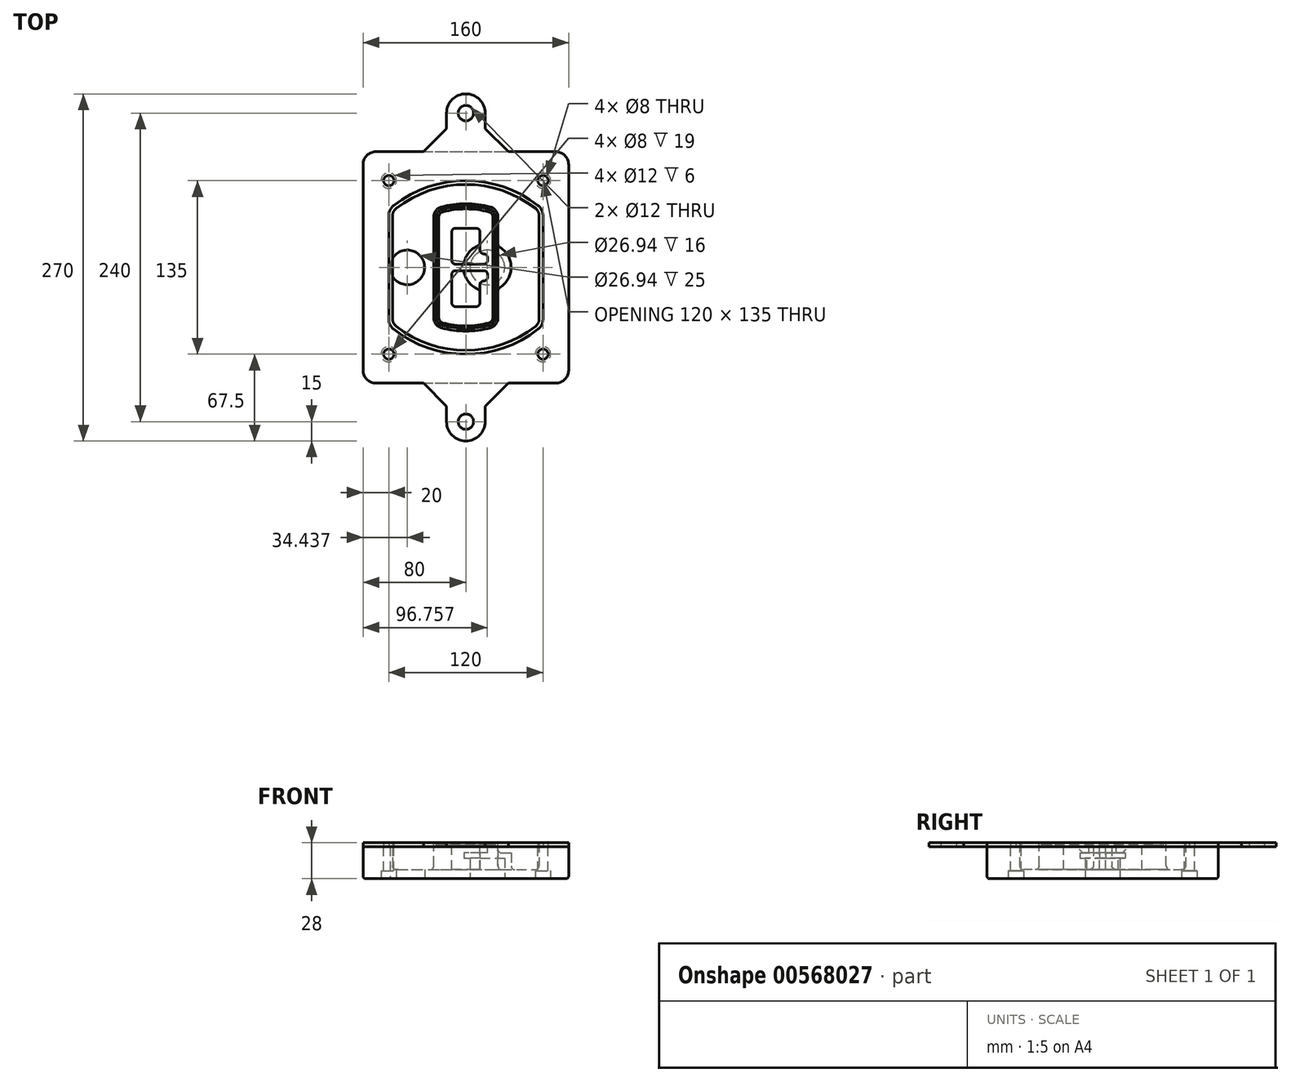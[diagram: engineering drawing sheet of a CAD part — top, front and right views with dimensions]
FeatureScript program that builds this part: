
annotation { "Feature Type Name" : "Feature", "Feature Type Description" : "" }
export const myFeature = defineFeature(function(context is Context, id is Id, definition is map)
    precondition{}
    {
        {
            var Q0;
            Q0=qCreatedBy(makeId("Top.planeOp"),FACE);
            var sketch = newSketch(context, id + "F0", { "sketchPlane" : qUnion([Q0])});
            skPoint(sketch, "E0.rect.middle", {"position": v(0, 0) * mm});
            skLineSegment(sketch, "E1.bottom", {"start": v(-70, -90) * mm, "end": v(70, -90) * mm});
            skLineSegment(sketch, "E1.top", {"start": v(-70, 90) * mm, "end": v(70, 90) * mm});
            skLineSegment(sketch, "E1.left", {"start": v(-80, -80) * mm, "end": v(-80, 80) * mm});
            skLineSegment(sketch, "E1.right", {"start": v(80, -80) * mm, "end": v(80, 80) * mm});
            skLineSegment(sketch, "E2", {"start": v(-80, 90) * mm, "end": v(80, -90) * mm, "construction": true});
            skLineSegment(sketch, "E3", {"start": v(80, 90) * mm, "end": v(-80, -90) * mm, "construction": true});
            skCircle(sketch, "E4", {"center": v(-60, 67.5) * mm, "radius": 4 * mm});
            skCircle(sketch, "E5", {"center": v(60, 67.5) * mm, "radius": 4 * mm});
            skCircle(sketch, "E6", {"center": v(60, -67.5) * mm, "radius": 4 * mm});
            skCircle(sketch, "E7", {"center": v(-60, -67.5) * mm, "radius": 4 * mm});
            skLineSegment(sketch, "E8", {"start": v(-60, 67.5) * mm, "end": v(60, 67.5) * mm, "construction": true});
            skLineSegment(sketch, "E9", {"start": v(60, 67.5) * mm, "end": v(60, -67.5) * mm, "construction": true});
            skLineSegment(sketch, "E10", {"start": v(60, -67.5) * mm, "end": v(-60, -67.5) * mm, "construction": true});
            skLineSegment(sketch, "E11", {"start": v(-60, -67.5) * mm, "end": v(-60, 67.5) * mm, "construction": true});
            skLineSegment(sketch, "E12", {"start": v(-60, 40.3) * mm, "end": v(-60, -40.3) * mm});
            skLineSegment(sketch, "E13", {"start": v(60, 40.3) * mm, "end": v(60, -40.3) * mm});
            skArc(sketch, "E14", {"start": v(56.15, 48.18) * mm, "mid": v(0, 67.5) * mm, "end": v(-56.15, 48.18) * mm});
            skArc(sketch, "E15", {"start": v(-56.15, -48.18) * mm, "mid": v(0, -67.5) * mm, "end": v(56.15, -48.18) * mm});
            skLineSegment(sketch, "E16", {"start": v(-60, 0) * mm, "end": v(60, 0) * mm, "construction": true});
            skPoint(sketch, "E17.visualSharp", {"position": v(-60, -45) * mm});
            skArc(sketch, "E17.filletArc", {"start": v(-60, -40.3) * mm, "mid": v(-58.99, -44.68) * mm, "end": v(-56.15, -48.18) * mm});
            skPoint(sketch, "E18.visualSharp", {"position": v(-60, 45) * mm});
            skArc(sketch, "E18.filletArc", {"start": v(-56.15, 48.18) * mm, "mid": v(-58.99, 44.68) * mm, "end": v(-60, 40.3) * mm});
            skPoint(sketch, "E19.visualSharp", {"position": v(60, 45) * mm});
            skArc(sketch, "E19.filletArc", {"start": v(60, 40.3) * mm, "mid": v(58.99, 44.68) * mm, "end": v(56.15, 48.18) * mm});
            skPoint(sketch, "E20.visualSharp", {"position": v(60, -45) * mm});
            skArc(sketch, "E20.filletArc", {"start": v(56.15, -48.18) * mm, "mid": v(58.99, -44.68) * mm, "end": v(60, -40.3) * mm});
            skPoint(sketch, "E21.visualSharp", {"position": v(-80, 90) * mm});
            skArc(sketch, "E21.filletArc", {"start": v(-70, 90) * mm, "mid": v(-77.07, 87.07) * mm, "end": v(-80, 80) * mm});
            skPoint(sketch, "E22.visualSharp", {"position": v(80, 90) * mm});
            skArc(sketch, "E22.filletArc", {"start": v(80, 80) * mm, "mid": v(77.07, 87.07) * mm, "end": v(70, 90) * mm});
            skPoint(sketch, "E23.visualSharp", {"position": v(80, -90) * mm});
            skArc(sketch, "E23.filletArc", {"start": v(70, -90) * mm, "mid": v(77.07, -87.07) * mm, "end": v(80, -80) * mm});
            skPoint(sketch, "E24.visualSharp", {"position": v(-80, -90) * mm});
            skArc(sketch, "E24.filletArc", {"start": v(-80, -80) * mm, "mid": v(-77.07, -87.07) * mm, "end": v(-70, -90) * mm});
            skArc(sketch, "E25.0", {"start": v(57, 40.3) * mm, "mid": v(56.3, 43.36) * mm, "end": v(54.3, 45.81) * mm});
            skLineSegment(sketch, "E25.1", {"start": v(57, 40.3) * mm, "end": v(57, -40.3) * mm});
            skArc(sketch, "E25.2", {"start": v(54.3, -45.81) * mm, "mid": v(56.3, -43.36) * mm, "end": v(57, -40.3) * mm});
            skArc(sketch, "E25.3", {"start": v(-54.3, -45.81) * mm, "mid": v(0, -64.5) * mm, "end": v(54.3, -45.81) * mm});
            skArc(sketch, "E25.4", {"start": v(-57, -40.3) * mm, "mid": v(-56.3, -43.36) * mm, "end": v(-54.3, -45.81) * mm});
            skArc(sketch, "E25.5", {"start": v(54.3, 45.81) * mm, "mid": v(0, 64.5) * mm, "end": v(-54.3, 45.81) * mm});
            skLineSegment(sketch, "E25.6", {"start": v(-57, 40.3) * mm, "end": v(-57, -40.3) * mm});
            skArc(sketch, "E25.7", {"start": v(-54.3, 45.81) * mm, "mid": v(-56.3, 43.36) * mm, "end": v(-57, 40.3) * mm});
            skArc(sketch, "E26.0", {"start": v(-58.62, 51.33) * mm, "mid": v(-62.58, 46.43) * mm, "end": v(-64, 40.3) * mm});
            skArc(sketch, "E26.1", {"start": v(58.62, 51.33) * mm, "mid": v(0, 71.5) * mm, "end": v(-58.62, 51.33) * mm});
            skArc(sketch, "E26.2", {"start": v(64, 40.3) * mm, "mid": v(62.58, 46.43) * mm, "end": v(58.62, 51.33) * mm});
            skLineSegment(sketch, "E26.3", {"start": v(64, 40.3) * mm, "end": v(64, -40.3) * mm});
            skArc(sketch, "E26.4", {"start": v(58.62, -51.33) * mm, "mid": v(62.58, -46.43) * mm, "end": v(64, -40.3) * mm});
            skLineSegment(sketch, "E26.5", {"start": v(-64, 40.3) * mm, "end": v(-64, -40.3) * mm});
            skArc(sketch, "E26.6", {"start": v(-58.62, -51.33) * mm, "mid": v(0, -71.5) * mm, "end": v(58.62, -51.33) * mm});
            skArc(sketch, "E26.7", {"start": v(-64, -40.3) * mm, "mid": v(-62.58, -46.43) * mm, "end": v(-58.62, -51.33) * mm});
            skSolve(sketch);
        }
        {
            var Q0;
            Q0=makeQuery(id+"F0.imprint","IMPRINT",FACE,{"disambiguationData":[TD([[makeQuery(id+"F0.imprint","IMPRINT",EDGE,{"derivedFrom":sQuery(id+"F0.wireOp",EDGE,"E1.bottom")}),1.0]])]});
            var Q1;
            Q1=makeQuery(id+"F0.imprint","IMPRINT",FACE,{"disambiguationData":[TD([[makeQuery(id+"F0.imprint","IMPRINT",EDGE,{"derivedFrom":sQuery(id+"F0.wireOp",EDGE,"E12")}),1.0]])]});
            var Q2;
            Q2=makeQuery(id+"F0.imprint","IMPRINT",FACE,{"disambiguationData":[TD([[makeQuery(id+"F0.imprint","IMPRINT",EDGE,{"derivedFrom":sQuery(id+"F0.wireOp",EDGE,"E25.0")}),1.0]])]});
            var Q3;
            Q3=makeQuery(id+"F0.imprint","IMPRINT",FACE,{"disambiguationData":[TD([[makeQuery(id+"F0.imprint","IMPRINT",EDGE,{"derivedFrom":sQuery(id+"F0.wireOp",EDGE,"E12")}),-1.0]])]});
            extrude(context, id + "F1", {"entities" : qUnion([Q0, Q1, Q2, Q3]), "oppositeDirection" : true, "depth" : 25 * mm});
        }
        {
            var Q0;
            Q0=makeQuery(id+"F0.imprint","IMPRINT",FACE,{"disambiguationData":[TD([[makeQuery(id+"F0.imprint","IMPRINT",EDGE,{"derivedFrom":sQuery(id+"F0.wireOp",EDGE,"E12")}),1.0]])]});
            extrude(context, id + "F2", {"entities" : qUnion([Q0]), "operationType" : NewBodyOperationType.ADD, "depth" : 3 * mm});
        }
        {
            var Q0;
            Q0=makeQuery(id+"F0.imprint","IMPRINT",FACE,{"disambiguationData":[TD([[makeQuery(id+"F0.imprint","IMPRINT",EDGE,{"derivedFrom":sQuery(id+"F0.wireOp",EDGE,"E25.0")}),1.0]])]});
            extrude(context, id + "F3", {"entities" : qUnion([Q0]), "operationType" : NewBodyOperationType.REMOVE, "oppositeDirection" : true, "depth" : 18 * mm});
        }
        {
            var Q0;
            Q0=makeQuery(id+"F2.opExtrude","CAP_FACE",FACE,{"disambiguationData":[OSD([sQuery(id+"F0.wireOp",EDGE,"E12"),sQuery(id+"F0.wireOp",EDGE,"E13"),sQuery(id+"F0.wireOp",EDGE,"E14"),sQuery(id+"F0.wireOp",EDGE,"E15"),sQuery(id+"F0.wireOp",EDGE,"E17.filletArc"),sQuery(id+"F0.wireOp",EDGE,"E18.filletArc"),sQuery(id+"F0.wireOp",EDGE,"E19.filletArc"),sQuery(id+"F0.wireOp",EDGE,"E20.filletArc"),sQuery(id+"F0.wireOp",EDGE,"E25.0"),sQuery(id+"F0.wireOp",EDGE,"E25.1"),sQuery(id+"F0.wireOp",EDGE,"E25.2"),sQuery(id+"F0.wireOp",EDGE,"E25.3"),sQuery(id+"F0.wireOp",EDGE,"E25.4"),sQuery(id+"F0.wireOp",EDGE,"E25.5"),sQuery(id+"F0.wireOp",EDGE,"E25.6"),sQuery(id+"F0.wireOp",EDGE,"E25.7")])],"isStart":false});
            var sketch = newSketch(context, id + "F4", { "sketchPlane" : qUnion([Q0])});
            skArc(sketch, "E27.0", {"start": v(-19.08, -46.97) * mm, "mid": v(0, -49.5) * mm, "end": v(19.08, -46.97) * mm});
            skArc(sketch, "E28.0", {"start": v(19.08, 46.97) * mm, "mid": v(0, 49.5) * mm, "end": v(-19.08, 46.97) * mm});
            skLineSegment(sketch, "E29", {"start": v(-25, 39.25) * mm, "end": v(-25, -39.25) * mm});
            skLineSegment(sketch, "E30", {"start": v(25, 39.25) * mm, "end": v(25, -39.25) * mm});
            skLineSegment(sketch, "E31", {"start": v(-25, 45.1) * mm, "end": v(25, 45.1) * mm, "construction": true});
            skLineSegment(sketch, "E32", {"start": v(-25, -45.1) * mm, "end": v(25, -45.1) * mm, "construction": true});
            skPoint(sketch, "E33.visualSharp", {"position": v(-25, 45.1) * mm});
            skArc(sketch, "E33.filletArc", {"start": v(-19.08, 46.97) * mm, "mid": v(-23.35, 44.11) * mm, "end": v(-25, 39.25) * mm});
            skPoint(sketch, "E34.visualSharp", {"position": v(25, 45.1) * mm});
            skArc(sketch, "E34.filletArc", {"start": v(25, 39.25) * mm, "mid": v(23.35, 44.11) * mm, "end": v(19.08, 46.97) * mm});
            skPoint(sketch, "E35.visualSharp", {"position": v(25, -45.1) * mm});
            skArc(sketch, "E35.filletArc", {"start": v(19.08, -46.97) * mm, "mid": v(23.35, -44.11) * mm, "end": v(25, -39.25) * mm});
            skPoint(sketch, "E36.visualSharp", {"position": v(-25, -45.1) * mm});
            skArc(sketch, "E36.filletArc", {"start": v(-25, -39.25) * mm, "mid": v(-23.35, -44.11) * mm, "end": v(-19.08, -46.97) * mm});
            skArc(sketch, "E37.0", {"start": v(54.3, 45.81) * mm, "mid": v(0, 64.5) * mm, "end": v(-54.3, 45.81) * mm});
            skArc(sketch, "E37.1", {"start": v(-54.3, 45.81) * mm, "mid": v(-56.3, 43.36) * mm, "end": v(-57, 40.3) * mm});
            skLineSegment(sketch, "E37.2", {"start": v(-57, 40.3) * mm, "end": v(-57, -40.3) * mm});
            skArc(sketch, "E37.3", {"start": v(-57, -40.3) * mm, "mid": v(-56.3, -43.36) * mm, "end": v(-54.3, -45.81) * mm});
            skArc(sketch, "E37.4", {"start": v(-54.3, -45.81) * mm, "mid": v(0, -64.5) * mm, "end": v(54.3, -45.81) * mm});
            skArc(sketch, "E37.5", {"start": v(54.3, -45.81) * mm, "mid": v(56.3, -43.36) * mm, "end": v(57, -40.3) * mm});
            skLineSegment(sketch, "E37.6", {"start": v(57, 40.3) * mm, "end": v(57, -40.3) * mm});
            skArc(sketch, "E37.7", {"start": v(57, 40.3) * mm, "mid": v(56.3, 43.36) * mm, "end": v(54.3, 45.81) * mm});
            skLineSegment(sketch, "E38.0", {"start": v(23, 39.25) * mm, "end": v(23, -39.25) * mm});
            skArc(sketch, "E38.1", {"start": v(18.56, -45.04) * mm, "mid": v(21.76, -42.9) * mm, "end": v(23, -39.25) * mm});
            skArc(sketch, "E38.2", {"start": v(-18.56, -45.04) * mm, "mid": v(0, -47.5) * mm, "end": v(18.56, -45.04) * mm});
            skArc(sketch, "E38.3", {"start": v(-23, -39.25) * mm, "mid": v(-21.76, -42.9) * mm, "end": v(-18.56, -45.04) * mm});
            skLineSegment(sketch, "E38.4", {"start": v(-23, 39.25) * mm, "end": v(-23, -39.25) * mm});
            skArc(sketch, "E38.5", {"start": v(23, 39.25) * mm, "mid": v(21.76, 42.9) * mm, "end": v(18.56, 45.04) * mm});
            skArc(sketch, "E38.6", {"start": v(-18.56, 45.04) * mm, "mid": v(-21.76, 42.9) * mm, "end": v(-23, 39.25) * mm});
            skArc(sketch, "E38.7", {"start": v(18.56, 45.04) * mm, "mid": v(0, 47.5) * mm, "end": v(-18.56, 45.04) * mm});
            skArc(sketch, "E39.0", {"start": v(21, 39.25) * mm, "mid": v(20.18, 41.68) * mm, "end": v(18.04, 43.1) * mm});
            skLineSegment(sketch, "E39.1", {"start": v(21, 39.25) * mm, "end": v(21, -39.25) * mm});
            skArc(sketch, "E39.2", {"start": v(18.04, -43.1) * mm, "mid": v(20.18, -41.68) * mm, "end": v(21, -39.25) * mm});
            skArc(sketch, "E39.3", {"start": v(-18.04, -43.1) * mm, "mid": v(0, -45.5) * mm, "end": v(18.04, -43.1) * mm});
            skArc(sketch, "E39.4", {"start": v(-21, -39.25) * mm, "mid": v(-20.18, -41.68) * mm, "end": v(-18.04, -43.1) * mm});
            skArc(sketch, "E39.5", {"start": v(18.04, 43.1) * mm, "mid": v(0, 45.5) * mm, "end": v(-18.04, 43.1) * mm});
            skLineSegment(sketch, "E39.6", {"start": v(-21, 39.25) * mm, "end": v(-21, -39.25) * mm});
            skArc(sketch, "E39.7", {"start": v(-18.04, 43.1) * mm, "mid": v(-20.18, 41.68) * mm, "end": v(-21, 39.25) * mm});
            skLineSegment(sketch, "E40", {"start": v(-25, 0) * mm, "end": v(25, 0) * mm, "construction": true});
            skLineSegment(sketch, "E41", {"start": v(-11, 5.5) * mm, "end": v(-11, 27.5) * mm});
            skLineSegment(sketch, "E42", {"start": v(-8, 30.5) * mm, "end": v(8, 30.5) * mm});
            skLineSegment(sketch, "E43", {"start": v(11, 27.5) * mm, "end": v(11, 13.5) * mm});
            skLineSegment(sketch, "E44", {"start": v(14, 10.5) * mm, "end": v(14, 10.5) * mm});
            skLineSegment(sketch, "E45", {"start": v(17, 7.5) * mm, "end": v(17, 5.5) * mm});
            skLineSegment(sketch, "E46", {"start": v(14, 2.5) * mm, "end": v(-8, 2.5) * mm});
            skPoint(sketch, "E47.visualSharp", {"position": v(-11, 30.5) * mm});
            skArc(sketch, "E47.filletArc", {"start": v(-8, 30.5) * mm, "mid": v(-10.12, 29.62) * mm, "end": v(-11, 27.5) * mm});
            skPoint(sketch, "E48.visualSharp", {"position": v(11, 30.5) * mm});
            skArc(sketch, "E48.filletArc", {"start": v(11, 27.5) * mm, "mid": v(10.12, 29.62) * mm, "end": v(8, 30.5) * mm});
            skPoint(sketch, "E49.visualSharp", {"position": v(11, 10.5) * mm});
            skArc(sketch, "E49.filletArc", {"start": v(11, 13.5) * mm, "mid": v(11.88, 11.38) * mm, "end": v(14, 10.5) * mm});
            skPoint(sketch, "E50.visualSharp", {"position": v(17, 10.5) * mm});
            skArc(sketch, "E50.filletArc", {"start": v(17, 7.5) * mm, "mid": v(16.12, 9.62) * mm, "end": v(14, 10.5) * mm});
            skPoint(sketch, "E51.visualSharp", {"position": v(17, 2.5) * mm});
            skArc(sketch, "E51.filletArc", {"start": v(14, 2.5) * mm, "mid": v(16.12, 3.38) * mm, "end": v(17, 5.5) * mm});
            skPoint(sketch, "E52.visualSharp", {"position": v(-11, 2.5) * mm});
            skArc(sketch, "E52.filletArc", {"start": v(-11, 5.5) * mm, "mid": v(-10.12, 3.38) * mm, "end": v(-8, 2.5) * mm});
            skLineSegment(sketch, "E53.0.MirrorCS", {"start": v(14, -2.5) * mm, "end": v(-8, -2.5) * mm});
            skArc(sketch, "E54.0.MirrorCS", {"start": v(-11, -5.5) * mm, "mid": v(-10.12, -3.38) * mm, "end": v(-8, -2.5) * mm});
            skLineSegment(sketch, "E55.0.MirrorCS", {"start": v(-11, -5.5) * mm, "end": v(-11, -27.5) * mm});
            skArc(sketch, "E56.0.MirrorCS", {"start": v(-8, -30.5) * mm, "mid": v(-10.12, -29.62) * mm, "end": v(-11, -27.5) * mm});
            skLineSegment(sketch, "E57.0.MirrorCS", {"start": v(-8, -30.5) * mm, "end": v(8, -30.5) * mm});
            skArc(sketch, "E58.0.MirrorCS", {"start": v(11, -27.5) * mm, "mid": v(10.12, -29.62) * mm, "end": v(8, -30.5) * mm});
            skLineSegment(sketch, "E59.0.MirrorCS", {"start": v(11, -27.5) * mm, "end": v(11, -13.5) * mm});
            skArc(sketch, "E60.0.MirrorCS", {"start": v(11, -13.5) * mm, "mid": v(11.88, -11.38) * mm, "end": v(14, -10.5) * mm});
            skArc(sketch, "E61.0.MirrorCS", {"start": v(17, -7.5) * mm, "mid": v(16.12, -9.62) * mm, "end": v(14, -10.5) * mm});
            skLineSegment(sketch, "E62.0.MirrorCS", {"start": v(17, -7.5) * mm, "end": v(17, -5.5) * mm});
            skArc(sketch, "E63.0.MirrorCS", {"start": v(14, -2.5) * mm, "mid": v(16.12, -3.38) * mm, "end": v(17, -5.5) * mm});
            skSolve(sketch);
        }
        {
            var Q0;
            Q0=makeQuery(id+"F4.imprint","IMPRINT",FACE,{"disambiguationData":[TD([[makeQuery(id+"F4.imprint","IMPRINT",EDGE,{"derivedFrom":sQuery(id+"F4.wireOp",EDGE,"E27.0")}),1.0]])]});
            var Q1;
            Q1=makeQuery(id+"F4.imprint","IMPRINT",FACE,{"disambiguationData":[TD([[makeQuery(id+"F4.imprint","IMPRINT",EDGE,{"derivedFrom":sQuery(id+"F4.wireOp",EDGE,"E38.0")}),-1.0]])]});
            var Q2;
            Q2=makeQuery(id+"F4.imprint","IMPRINT",FACE,{"disambiguationData":[TD([[makeQuery(id+"F4.imprint","IMPRINT",EDGE,{"derivedFrom":sQuery(id+"F4.wireOp",EDGE,"E39.0")}),1.0]])]});
            extrude(context, id + "F5", {"entities" : qUnion([Q0, Q1, Q2]), "operationType" : NewBodyOperationType.ADD, "endBound" : BoundingType.UP_TO_NEXT, "oppositeDirection" : true, "depth" : 25 * mm});
        }
        {
            var Q0;
            Q0=makeQuery(id+"F4.imprint","IMPRINT",FACE,{"disambiguationData":[TD([[makeQuery(id+"F4.imprint","IMPRINT",EDGE,{"derivedFrom":sQuery(id+"F4.wireOp",EDGE,"E38.0")}),-1.0]])]});
            extrude(context, id + "F6", {"entities" : qUnion([Q0]), "operationType" : NewBodyOperationType.REMOVE, "oppositeDirection" : true, "depth" : 2 * mm});
        }
        {
            var Q0;
            Q0=makeQuery(id+"F1.opExtrude","CAP_FACE",FACE,{"disambiguationData":[OSD([sQuery(id+"F0.wireOp",EDGE,"E1.bottom"),sQuery(id+"F0.wireOp",EDGE,"E1.top"),sQuery(id+"F0.wireOp",EDGE,"E1.left"),sQuery(id+"F0.wireOp",EDGE,"E1.right"),sQuery(id+"F0.wireOp",EDGE,"E4"),sQuery(id+"F0.wireOp",EDGE,"E5"),sQuery(id+"F0.wireOp",EDGE,"E6"),sQuery(id+"F0.wireOp",EDGE,"E7"),sQuery(id+"F0.wireOp",EDGE,"E21.filletArc"),sQuery(id+"F0.wireOp",EDGE,"E22.filletArc"),sQuery(id+"F0.wireOp",EDGE,"E23.filletArc"),sQuery(id+"F0.wireOp",EDGE,"E24.filletArc")])],"isStart":false});
            var sketch = newSketch(context, id + "F7", { "sketchPlane" : qUnion([Q0])});
            skCircle(sketch, "E64", {"center": v(16.76, 0) * mm, "radius": 13.47 * mm});
            skCircle(sketch, "E65", {"center": v(-45.56, 0) * mm, "radius": 13.47 * mm});
            skLineSegment(sketch, "E66", {"start": v(80, 0) * mm, "end": v(-80, 0) * mm});
            skCircle(sketch, "E67", {"center": v(16.76, 0) * mm, "radius": 18.47 * mm});
            skCircle(sketch, "E68", {"center": v(60, -67.5) * mm, "radius": 6 * mm});
            skCircle(sketch, "E69", {"center": v(-60, -67.5) * mm, "radius": 6 * mm});
            skCircle(sketch, "E70", {"center": v(-60, 67.5) * mm, "radius": 6 * mm});
            skCircle(sketch, "E71", {"center": v(60, 67.5) * mm, "radius": 6 * mm});
            skSolve(sketch);
        }
        {
            var Q0;
            {var subQ1=sQuery(id+"F7.wireOp",EDGE,"E66");var subQ4=sQuery(id+"F7.wireOp",EDGE,"E64");var subQ6=makeQuery(id+"F7.imprint","INTERSECT",VERTEX,{"disambiguationData":[OD(0.0)],"derivedFrom":[subQ4,subQ1]});Q0=makeQuery(id+"F7.imprint","IMPRINT",FACE,{"disambiguationData":[TD([[makeQuery(id+"F7.imprint","IMPRINT",EDGE,{"disambiguationData":[TD([[subQ6,-1.0]])],"derivedFrom":subQ4}),-1.0]])]});}
            var Q1;
            {var subQ0=sQuery(id+"F7.wireOp",EDGE,"E66");var subQ1=sQuery(id+"F7.wireOp",EDGE,"E64");var subQ3=makeQuery(id+"F7.imprint","INTERSECT",VERTEX,{"disambiguationData":[OD(0.0)],"derivedFrom":[subQ1,subQ0]});Q1=makeQuery(id+"F7.imprint","IMPRINT",FACE,{"disambiguationData":[TD([[makeQuery(id+"F7.imprint","IMPRINT",EDGE,{"disambiguationData":[TD([[subQ3,-1.0]])],"derivedFrom":subQ1}),1.0]])]});}
            var Q2;
            {var subQ0=sQuery(id+"F7.wireOp",EDGE,"E66");var subQ1=sQuery(id+"F7.wireOp",EDGE,"E64");var subQ3=makeQuery(id+"F7.imprint","INTERSECT",VERTEX,{"disambiguationData":[OD(0.0)],"derivedFrom":[subQ1,subQ0]});Q2=makeQuery(id+"F7.imprint","IMPRINT",FACE,{"disambiguationData":[TD([[makeQuery(id+"F7.imprint","IMPRINT",EDGE,{"disambiguationData":[TD([[subQ3,1.0]])],"derivedFrom":subQ1}),1.0]])]});}
            var Q3;
            {var subQ1=sQuery(id+"F7.wireOp",EDGE,"E66");var subQ4=sQuery(id+"F7.wireOp",EDGE,"E64");var subQ6=makeQuery(id+"F7.imprint","INTERSECT",VERTEX,{"disambiguationData":[OD(0.0)],"derivedFrom":[subQ4,subQ1]});Q3=makeQuery(id+"F7.imprint","IMPRINT",FACE,{"disambiguationData":[TD([[makeQuery(id+"F7.imprint","IMPRINT",EDGE,{"disambiguationData":[TD([[subQ6,1.0]])],"derivedFrom":subQ4}),-1.0]])]});}
            extrude(context, id + "F8", {"entities" : qUnion([Q0, Q1, Q2, Q3]), "operationType" : NewBodyOperationType.ADD, "oppositeDirection" : true, "depth" : 20 * mm});
        }
        {
            var Q0;
            {var subQ0=sQuery(id+"F7.wireOp",EDGE,"E66");var subQ1=sQuery(id+"F7.wireOp",EDGE,"E64");var subQ3=makeQuery(id+"F7.imprint","INTERSECT",VERTEX,{"disambiguationData":[OD(0.0)],"derivedFrom":[subQ1,subQ0]});Q0=makeQuery(id+"F7.imprint","IMPRINT",FACE,{"disambiguationData":[TD([[makeQuery(id+"F7.imprint","IMPRINT",EDGE,{"disambiguationData":[TD([[subQ3,-1.0]])],"derivedFrom":subQ1}),1.0]])]});}
            var Q1;
            {var subQ0=sQuery(id+"F7.wireOp",EDGE,"E66");var subQ1=sQuery(id+"F7.wireOp",EDGE,"E64");var subQ3=makeQuery(id+"F7.imprint","INTERSECT",VERTEX,{"disambiguationData":[OD(0.0)],"derivedFrom":[subQ1,subQ0]});Q1=makeQuery(id+"F7.imprint","IMPRINT",FACE,{"disambiguationData":[TD([[makeQuery(id+"F7.imprint","IMPRINT",EDGE,{"disambiguationData":[TD([[subQ3,1.0]])],"derivedFrom":subQ1}),1.0]])]});}
            extrude(context, id + "F9", {"entities" : qUnion([Q0, Q1]), "operationType" : NewBodyOperationType.REMOVE, "oppositeDirection" : true, "depth" : 16 * mm});
        }
        {
            var Q0;
            {var subQ0=sQuery(id+"F7.wireOp",EDGE,"E66");var subQ1=sQuery(id+"F7.wireOp",EDGE,"E65");var subQ3=makeQuery(id+"F7.imprint","INTERSECT",VERTEX,{"disambiguationData":[OD(0.0)],"derivedFrom":[subQ1,subQ0]});Q0=makeQuery(id+"F7.imprint","IMPRINT",FACE,{"disambiguationData":[TD([[makeQuery(id+"F7.imprint","IMPRINT",EDGE,{"disambiguationData":[TD([[subQ3,-1.0]])],"derivedFrom":subQ1}),1.0]])]});}
            var Q1;
            {var subQ0=sQuery(id+"F7.wireOp",EDGE,"E66");var subQ1=sQuery(id+"F7.wireOp",EDGE,"E65");var subQ3=makeQuery(id+"F7.imprint","INTERSECT",VERTEX,{"disambiguationData":[OD(0.0)],"derivedFrom":[subQ1,subQ0]});Q1=makeQuery(id+"F7.imprint","IMPRINT",FACE,{"disambiguationData":[TD([[makeQuery(id+"F7.imprint","IMPRINT",EDGE,{"disambiguationData":[TD([[subQ3,1.0]])],"derivedFrom":subQ1}),1.0]])]});}
            extrude(context, id + "F10", {"entities" : qUnion([Q0, Q1]), "operationType" : NewBodyOperationType.REMOVE, "oppositeDirection" : true, "depth" : 25 * mm});
        }
        {
            var Q0;
            Q0=makeQuery(id+"F7.imprint","IMPRINT",FACE,{"disambiguationData":[TD([[makeQuery(id+"F7.imprint","IMPRINT",EDGE,{"derivedFrom":sQuery(id+"F7.wireOp",EDGE,"E68")}),1.0]])]});
            var Q1;
            Q1=makeQuery(id+"F7.imprint","IMPRINT",FACE,{"disambiguationData":[TD([[makeQuery(id+"F7.imprint","IMPRINT",EDGE,{"derivedFrom":makeQuery(id+"F1.opExtrude","CAP_EDGE",EDGE,{"disambiguationData":[OSD([sQuery(id+"F0.wireOp",EDGE,"E5")])],"isStart":false})}),-1.0]])]});
            var Q2;
            Q2=makeQuery(id+"F7.imprint","IMPRINT",FACE,{"disambiguationData":[TD([[makeQuery(id+"F7.imprint","IMPRINT",EDGE,{"derivedFrom":sQuery(id+"F7.wireOp",EDGE,"E69")}),1.0]])]});
            var Q3;
            Q3=makeQuery(id+"F7.imprint","IMPRINT",FACE,{"disambiguationData":[TD([[makeQuery(id+"F7.imprint","IMPRINT",EDGE,{"derivedFrom":makeQuery(id+"F1.opExtrude","CAP_EDGE",EDGE,{"disambiguationData":[OSD([sQuery(id+"F0.wireOp",EDGE,"E4")])],"isStart":false})}),-1.0]])]});
            var Q4;
            Q4=makeQuery(id+"F7.imprint","IMPRINT",FACE,{"disambiguationData":[TD([[makeQuery(id+"F7.imprint","IMPRINT",EDGE,{"derivedFrom":sQuery(id+"F7.wireOp",EDGE,"E70")}),1.0]])]});
            var Q5;
            Q5=makeQuery(id+"F7.imprint","IMPRINT",FACE,{"disambiguationData":[TD([[makeQuery(id+"F7.imprint","IMPRINT",EDGE,{"derivedFrom":makeQuery(id+"F1.opExtrude","CAP_EDGE",EDGE,{"disambiguationData":[OSD([sQuery(id+"F0.wireOp",EDGE,"E7")])],"isStart":false})}),-1.0]])]});
            var Q6;
            Q6=makeQuery(id+"F7.imprint","IMPRINT",FACE,{"disambiguationData":[TD([[makeQuery(id+"F7.imprint","IMPRINT",EDGE,{"derivedFrom":sQuery(id+"F7.wireOp",EDGE,"E71")}),1.0]])]});
            var Q7;
            Q7=makeQuery(id+"F7.imprint","IMPRINT",FACE,{"disambiguationData":[TD([[makeQuery(id+"F7.imprint","IMPRINT",EDGE,{"derivedFrom":makeQuery(id+"F1.opExtrude","CAP_EDGE",EDGE,{"disambiguationData":[OSD([sQuery(id+"F0.wireOp",EDGE,"E6")])],"isStart":false})}),-1.0]])]});
            extrude(context, id + "F11", {"entities" : qUnion([Q0, Q1, Q2, Q3, Q4, Q5, Q6, Q7]), "operationType" : NewBodyOperationType.REMOVE, "oppositeDirection" : true, "depth" : 6 * mm});
        }
        {
            var Q0;
            Q0=makeQuery(id+"F9.boolean.opBoolean","COPY",FACE,{"derivedFrom":makeQuery(id+"F9.opExtrude","CAP_FACE",FACE,{"disambiguationData":[OSD([sQuery(id+"F7.wireOp",EDGE,"E64")])],"isStart":false})});
            var sketch = newSketch(context, id + "F12", { "sketchPlane" : qUnion([Q0])});
            skArc(sketch, "E72.0", {"start": v(11, 17.55) * mm, "mid": v(2.57, 11.82) * mm, "end": v(-1.54, 2.5) * mm});
            skArc(sketch, "E72.1", {"start": v(-1.54, -2.5) * mm, "mid": v(2.57, -11.82) * mm, "end": v(11, -17.55) * mm});
            skLineSegment(sketch, "E73", {"start": v(-1.54, -2.5) * mm, "end": v(14, -2.5) * mm});
            skLineSegment(sketch, "E74.0", {"start": v(14, 2.5) * mm, "end": v(-1.54, 2.5) * mm});
            skArc(sketch, "E74.1", {"start": v(14, 2.5) * mm, "mid": v(16.12, 3.38) * mm, "end": v(17, 5.5) * mm});
            skLineSegment(sketch, "E74.2", {"start": v(17, 7.5) * mm, "end": v(17, 5.5) * mm});
            skArc(sketch, "E74.3", {"start": v(17, 7.5) * mm, "mid": v(16.12, 9.62) * mm, "end": v(14, 10.5) * mm});
            skArc(sketch, "E74.4", {"start": v(11, 13.5) * mm, "mid": v(11.88, 11.38) * mm, "end": v(14, 10.5) * mm});
            skLineSegment(sketch, "E74.5", {"start": v(11, 17.55) * mm, "end": v(11, 13.5) * mm});
            skLineSegment(sketch, "E74.7", {"start": v(14, -2.5) * mm, "end": v(-1.54, -2.5) * mm});
            skArc(sketch, "E74.8", {"start": v(14, -2.5) * mm, "mid": v(16.12, -3.38) * mm, "end": v(17, -5.5) * mm});
            skLineSegment(sketch, "E74.9", {"start": v(17, -7.5) * mm, "end": v(17, -5.5) * mm});
            skArc(sketch, "E74.10", {"start": v(17, -7.5) * mm, "mid": v(16.12, -9.62) * mm, "end": v(14, -10.5) * mm});
            skArc(sketch, "E74.11", {"start": v(11, -13.5) * mm, "mid": v(11.88, -11.38) * mm, "end": v(14, -10.5) * mm});
            skLineSegment(sketch, "E74.12", {"start": v(11, -17.55) * mm, "end": v(11, -13.5) * mm});
            skPoint(sketch, "E75.orphan", {"position": v(11, -27.5) * mm});
            skPoint(sketch, "E76.orphan", {"position": v(-8, -2.5) * mm});
            skPoint(sketch, "E77.orphan", {"position": v(-8, 2.5) * mm});
            skPoint(sketch, "E78.orphan", {"position": v(11, 27.5) * mm});
            skSolve(sketch);
        }
        {
            var Q0;
            {var subQ7=sQuery(id+"F12.wireOp",EDGE,"E72.0");var subQ14=sQuery(id+"F12.wireOp",EDGE,"E72.1");var subQ16=sQuery(id+"F12.wireOp",EDGE,"E74.1");var subQ18=sQuery(id+"F12.wireOp",EDGE,"E74.8");Q0=qUnion([makeQuery(id+"F12.imprint","IMPRINT",FACE,{"disambiguationData":[TD([[makeQuery(id+"F12.imprint","IMPRINT",EDGE,{"derivedFrom":subQ7}),1.0]])]}),makeQuery(id+"F12.imprint","IMPRINT",FACE,{"disambiguationData":[TD([[makeQuery(id+"F12.imprint","IMPRINT",EDGE,{"derivedFrom":subQ14}),1.0]])]}),makeQuery(id+"F12.imprint","IMPRINT",FACE,{"disambiguationData":[TD([[makeQuery(id+"F12.imprint","IMPRINT",EDGE,{"derivedFrom":subQ16}),1.0]])]}),makeQuery(id+"F12.imprint","IMPRINT",FACE,{"disambiguationData":[TD([[makeQuery(id+"F12.imprint","IMPRINT",EDGE,{"derivedFrom":subQ18}),-1.0]])]})]);}
            var Q1;
            Q1=makeQuery(id+"F5.boolean.opBoolean","SPLIT",FACE,{"disambiguationData":[TD([makeQuery(id+"F5.opExtrude","SWEPT_FACE",FACE,{"disambiguationData":[OSD([sQuery(id+"F4.wireOp",EDGE,"E41")])]})])],"derivedFrom":makeQuery(id+"F3.boolean.opBoolean","COPY",FACE,{"derivedFrom":makeQuery(id+"F3.opExtrude","CAP_FACE",FACE,{"disambiguationData":[OSD([sQuery(id+"F0.wireOp",EDGE,"E25.0"),sQuery(id+"F0.wireOp",EDGE,"E25.1"),sQuery(id+"F0.wireOp",EDGE,"E25.2"),sQuery(id+"F0.wireOp",EDGE,"E25.3"),sQuery(id+"F0.wireOp",EDGE,"E25.4"),sQuery(id+"F0.wireOp",EDGE,"E25.5"),sQuery(id+"F0.wireOp",EDGE,"E25.6"),sQuery(id+"F0.wireOp",EDGE,"E25.7")])],"isStart":false})})});
            extrude(context, id + "F13", {"entities" : qUnion([Q0]), "operationType" : NewBodyOperationType.REMOVE, "endBound" : BoundingType.UP_TO_SURFACE, "endBoundEntityFace" : qUnion([Q1]), "depth" : 25 * mm});
        }
        {
            var Q0;
            Q0=makeQuery(id+"F3.boolean.opBoolean","COPY",EDGE,{"derivedFrom":makeQuery(id+"F3.opExtrude","CAP_EDGE",EDGE,{"disambiguationData":[OSD([sQuery(id+"F0.wireOp",EDGE,"E25.6")])],"isStart":false})});
            var Q1;
            Q1=makeQuery(id+"F8.boolean.opBoolean","INTERSECT",EDGE,{"derivedFrom":[makeQuery(id+"F5.opExtrude","SWEPT_FACE",FACE,{"disambiguationData":[OSD([sQuery(id+"F4.wireOp",EDGE,"E30")])]}),makeQuery(id+"F8.opExtrude","CAP_FACE",FACE,{"disambiguationData":[OSD([sQuery(id+"F7.wireOp",EDGE,"E67")])],"isStart":false})]});
            var Q2;
            Q2=makeQuery(id+"F8.boolean.opBoolean","INTERSECT",EDGE,{"disambiguationData":[OD(1.0)],"derivedFrom":[makeQuery(id+"F5.opExtrude","SWEPT_FACE",FACE,{"disambiguationData":[OSD([sQuery(id+"F4.wireOp",EDGE,"E30")])]}),makeQuery(id+"F8.opExtrude","SWEPT_FACE",FACE,{"disambiguationData":[OSD([sQuery(id+"F7.wireOp",EDGE,"E67")])]})]});
            var Q3;
            {var subQ0=sQuery(id+"F4.wireOp",EDGE,"E30");Q3=makeQuery(id+"F8.boolean.opBoolean","SPLIT",EDGE,{"disambiguationData":[TD([makeQuery(id+"F5.opExtrude","SWEPT_FACE",FACE,{"disambiguationData":[OSD([sQuery(id+"F4.wireOp",EDGE,"E35.filletArc")])]})])],"derivedFrom":makeQuery(id+"F5.opExtrude","CAP_EDGE",EDGE,{"disambiguationData":[OSD([subQ0])],"isStart":false})});}
            var Q4;
            {var subQ0=sQuery(id+"F0.wireOp",EDGE,"E25.7");var subQ1=sQuery(id+"F0.wireOp",EDGE,"E25.1");var subQ2=sQuery(id+"F0.wireOp",EDGE,"E25.6");var subQ3=sQuery(id+"F0.wireOp",EDGE,"E25.5");var subQ4=sQuery(id+"F0.wireOp",EDGE,"E25.4");var subQ5=sQuery(id+"F0.wireOp",EDGE,"E25.0");var subQ6=sQuery(id+"F0.wireOp",EDGE,"E25.2");var subQ7=sQuery(id+"F0.wireOp",EDGE,"E25.3");Q4=makeQuery(id+"F8.boolean.opBoolean","INTERSECT",EDGE,{"derivedFrom":[makeQuery(id+"F5.boolean.opBoolean","SPLIT",FACE,{"disambiguationData":[TD([makeQuery(id+"F2.opExtrude","SWEPT_FACE",FACE,{"disambiguationData":[OSD([subQ5])]})])],"derivedFrom":makeQuery(id+"F3.boolean.opBoolean","COPY",FACE,{"derivedFrom":makeQuery(id+"F3.opExtrude","CAP_FACE",FACE,{"disambiguationData":[OSD([subQ5,subQ1,subQ6,subQ7,subQ4,subQ3,subQ2,subQ0])],"isStart":false})})}),makeQuery(id+"F8.opExtrude","SWEPT_FACE",FACE,{"disambiguationData":[OSD([sQuery(id+"F7.wireOp",EDGE,"E67")])]})]});}
            var Q5;
            Q5=makeQuery(id+"F8.boolean.opBoolean","INTERSECT",EDGE,{"disambiguationData":[OD(0.0)],"derivedFrom":[makeQuery(id+"F5.opExtrude","SWEPT_FACE",FACE,{"disambiguationData":[OSD([sQuery(id+"F4.wireOp",EDGE,"E30")])]}),makeQuery(id+"F8.opExtrude","SWEPT_FACE",FACE,{"disambiguationData":[OSD([sQuery(id+"F7.wireOp",EDGE,"E67")])]})]});
            fillet(context, id + "F14", {"entities" : qUnion([Q0, Q1, Q2, Q3, Q4, Q5]), "radius" : 3 * mm, "tangentPropagation" : true, "allowEdgeOverflow" : false});
        }
        {
            var Q0;
            Q0=makeQuery(id+"F1.opExtrude","CAP_EDGE",EDGE,{"disambiguationData":[OSD([sQuery(id+"F0.wireOp",EDGE,"E1.bottom")])],"isStart":false});
            fillet(context, id + "F15", {"entities" : qUnion([Q0]), "radius" : 2 * mm, "tangentPropagation" : true, "allowEdgeOverflow" : false});
        }
        {
            var Q0;
            {var subQ0=sQuery(id+"F0.wireOp",EDGE,"E21.filletArc");var subQ1=sQuery(id+"F0.wireOp",EDGE,"E7");var subQ2=sQuery(id+"F0.wireOp",EDGE,"E6");var subQ3=sQuery(id+"F0.wireOp",EDGE,"E5");var subQ4=sQuery(id+"F0.wireOp",EDGE,"E4");var subQ5=sQuery(id+"F0.wireOp",EDGE,"E22.filletArc");var subQ6=sQuery(id+"F0.wireOp",EDGE,"E1.bottom");var subQ7=sQuery(id+"F0.wireOp",EDGE,"E1.right");var subQ8=sQuery(id+"F0.wireOp",EDGE,"E1.top");var subQ9=sQuery(id+"F0.wireOp",EDGE,"E1.left");var subQ10=sQuery(id+"F0.wireOp",EDGE,"E23.filletArc");var subQ11=sQuery(id+"F0.wireOp",EDGE,"E24.filletArc");Q0=makeQuery(id+"F2.boolean.opBoolean","SPLIT",FACE,{"disambiguationData":[TD([makeQuery(id+"F1.opExtrude","SWEPT_FACE",FACE,{"disambiguationData":[OSD([subQ6])]})])],"derivedFrom":makeQuery(id+"F1.opExtrude","CAP_FACE",FACE,{"disambiguationData":[OSD([subQ6,subQ8,subQ9,subQ7,subQ4,subQ3,subQ2,subQ1,subQ0,subQ5,subQ10,subQ11])],"isStart":true})});}
            var sketch = newSketch(context, id + "F16", { "sketchPlane" : qUnion([Q0])});
            skLineSegment(sketch, "E79", {"start": v(0, 90) * mm, "end": v(0, 120) * mm, "construction": true});
            skCircle(sketch, "E80", {"center": v(0, 120) * mm, "radius": 6 * mm});
            skArc(sketch, "E81", {"start": v(15, 120) * mm, "mid": v(0, 135) * mm, "end": v(-15, 120) * mm});
            skLineSegment(sketch, "E82", {"start": v(-15, 120) * mm, "end": v(-15, 108) * mm});
            skLineSegment(sketch, "E83", {"start": v(15, 120) * mm, "end": v(15, 108) * mm});
            skLineSegment(sketch, "E84", {"start": v(15, 108) * mm, "end": v(33, 90) * mm});
            skLineSegment(sketch, "E85", {"start": v(-15, 108) * mm, "end": v(-33, 90) * mm});
            skLineSegment(sketch, "E86", {"start": v(-80, 0) * mm, "end": v(80, 0) * mm, "construction": true});
            skLineSegment(sketch, "E87.MirrorCS", {"start": v(15, -108) * mm, "end": v(33, -90) * mm});
            skLineSegment(sketch, "E88.MirrorCS", {"start": v(15, -120) * mm, "end": v(15, -108) * mm});
            skArc(sketch, "E89.MirrorCS", {"start": v(15, -120) * mm, "mid": v(0, -135) * mm, "end": v(-15, -120) * mm});
            skLineSegment(sketch, "E90.MirrorCS", {"start": v(-15, -120) * mm, "end": v(-15, -108) * mm});
            skLineSegment(sketch, "E91.MirrorCS", {"start": v(-15, -108) * mm, "end": v(-33, -90) * mm});
            skCircle(sketch, "E92.MirrorC", {"center": v(0, -120) * mm, "radius": 6 * mm});
            skLineSegment(sketch, "E93.MirrorCS", {"start": v(0, -90) * mm, "end": v(0, -120) * mm, "construction": true});
            skSolve(sketch);
        }
        {
            var Q0;
            {var subQ0=sQuery(id+"F16.wireOp",EDGE,"E87.MirrorCS");Q0=makeQuery(id+"F16.imprint","IMPRINT",FACE,{"disambiguationData":[TD([[makeQuery(id+"F16.imprint","IMPRINT",EDGE,{"derivedFrom":subQ0}),1.0]])]});}
            var Q1;
            Q1=makeQuery(id+"F16.imprint","IMPRINT",FACE,{"disambiguationData":[TD([[makeQuery(id+"F16.imprint","IMPRINT",EDGE,{"derivedFrom":makeQuery(id+"F1.opExtrude","CAP_EDGE",EDGE,{"disambiguationData":[OSD([sQuery(id+"F0.wireOp",EDGE,"E1.left")])],"isStart":true})}),-1.0]])]});
            var Q2;
            Q2=makeQuery(id+"F16.imprint","IMPRINT",FACE,{"disambiguationData":[TD([[makeQuery(id+"F16.imprint","IMPRINT",EDGE,{"derivedFrom":sQuery(id+"F16.wireOp",EDGE,"E80")}),-1.0]])]});
            var Q3;
            Q3=makeQuery(id+"F2.opExtrude","CAP_FACE",FACE,{"disambiguationData":[OSD([sQuery(id+"F0.wireOp",EDGE,"E12"),sQuery(id+"F0.wireOp",EDGE,"E13"),sQuery(id+"F0.wireOp",EDGE,"E14"),sQuery(id+"F0.wireOp",EDGE,"E15"),sQuery(id+"F0.wireOp",EDGE,"E17.filletArc"),sQuery(id+"F0.wireOp",EDGE,"E18.filletArc"),sQuery(id+"F0.wireOp",EDGE,"E19.filletArc"),sQuery(id+"F0.wireOp",EDGE,"E20.filletArc"),sQuery(id+"F0.wireOp",EDGE,"E25.0"),sQuery(id+"F0.wireOp",EDGE,"E25.1"),sQuery(id+"F0.wireOp",EDGE,"E25.2"),sQuery(id+"F0.wireOp",EDGE,"E25.3"),sQuery(id+"F0.wireOp",EDGE,"E25.4"),sQuery(id+"F0.wireOp",EDGE,"E25.5"),sQuery(id+"F0.wireOp",EDGE,"E25.6"),sQuery(id+"F0.wireOp",EDGE,"E25.7")])],"isStart":false});
            extrude(context, id + "F17", {"entities" : qUnion([Q0, Q1, Q2]), "endBound" : BoundingType.UP_TO_SURFACE, "depth" : 25 * mm, "endBoundEntityFace" : qUnion([Q3]), "offsetDistance" : 25 * mm});
        }
    });
